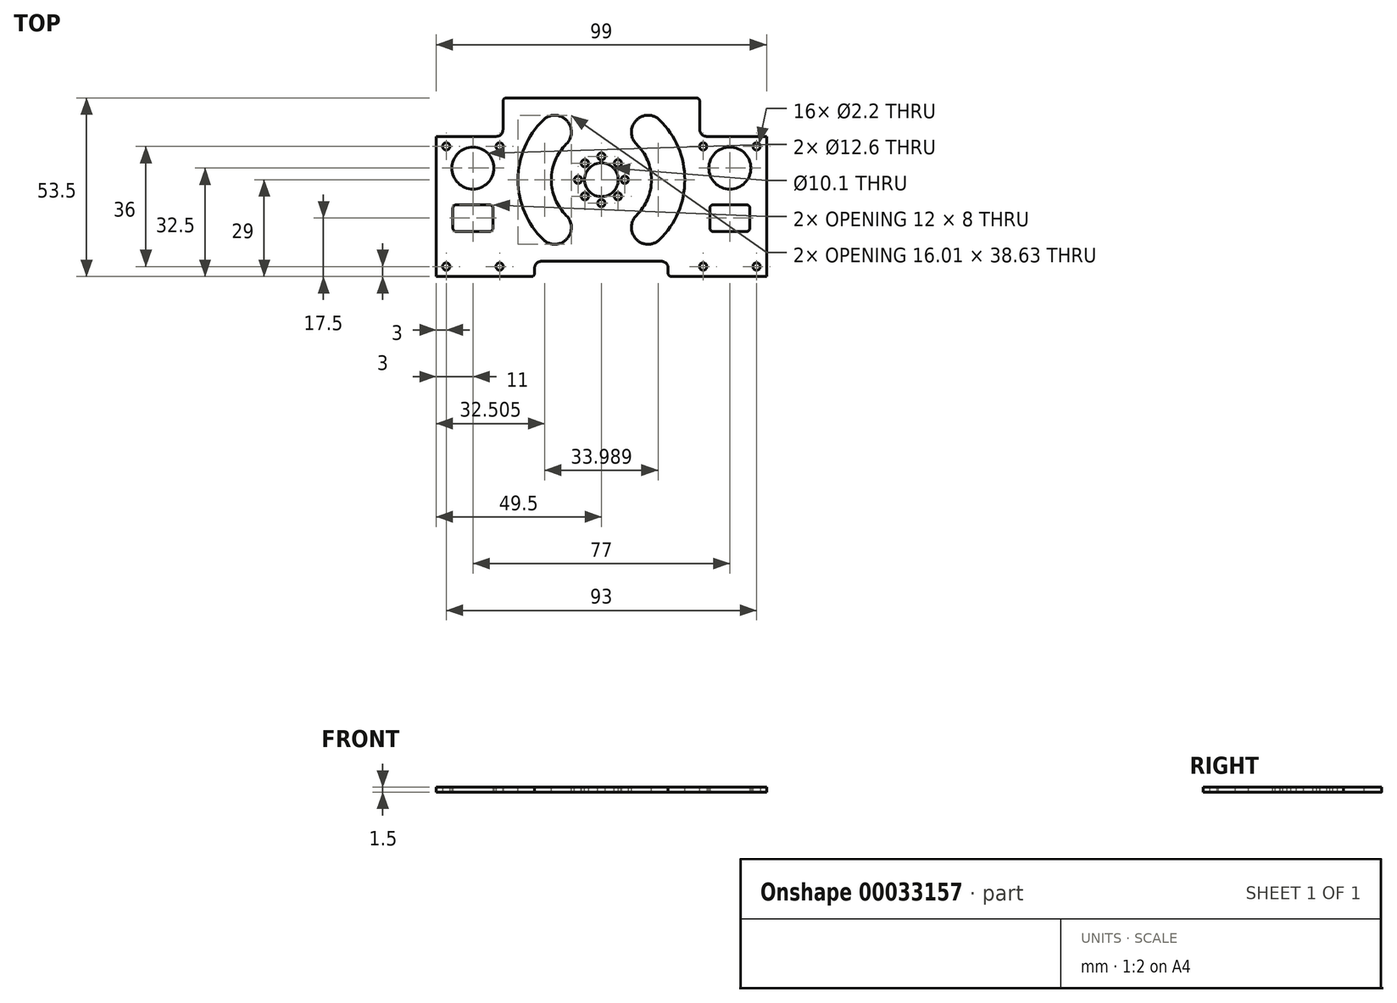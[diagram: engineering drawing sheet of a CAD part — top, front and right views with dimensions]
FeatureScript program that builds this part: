
annotation { "Feature Type Name" : "Feature", "Feature Type Description" : "" }
export const myFeature = defineFeature(function(context is Context, id is Id, definition is map)
    precondition{}
    {
        {
            var Q0;
            Q0=qCreatedBy(makeId("Top.planeOp"),FACE);
            var sketch = newSketch(context, id + "F0", { "sketchPlane" : qUnion([Q0])});
            skLineSegment(sketch, "E0.bottom", {"start": v(-49.5, 35) * mm, "end": v(49.5, 35) * mm});
            skLineSegment(sketch, "E0.top", {"start": v(-49.5, -35) * mm, "end": v(49.5, -35) * mm});
            skLineSegment(sketch, "E0.left", {"start": v(-49.5, 35) * mm, "end": v(-49.5, -35) * mm});
            skLineSegment(sketch, "E0.right", {"start": v(49.5, 35) * mm, "end": v(49.5, -35) * mm});
            skPoint(sketch, "E0.middle", {"position": v(0, 0) * mm});
            skLineSegment(sketch, "E1", {"start": v(-38.5, 35) * mm, "end": v(-38.5, -35) * mm, "construction": true});
            skCircle(sketch, "E2", {"center": v(-46.5, 10) * mm, "radius": 1.1 * mm});
            skCircle(sketch, "E3", {"center": v(-46.5, -26) * mm, "radius": 1.1 * mm});
            skCircle(sketch, "E4.MirrorC", {"center": v(-30.5, 10) * mm, "radius": 1.1 * mm});
            skCircle(sketch, "E5.MirrorC", {"center": v(-30.5, -26) * mm, "radius": 1.1 * mm});
            skCircle(sketch, "E6", {"center": v(-38.5, 3.5) * mm, "radius": 6.3 * mm});
            skCircle(sketch, "E7.MirrorC", {"center": v(30.5, -26) * mm, "radius": 1.1 * mm});
            skCircle(sketch, "E8.MirrorC", {"center": v(38.5, 3.5) * mm, "radius": 6.3 * mm});
            skCircle(sketch, "E9.MirrorC", {"center": v(30.5, 10) * mm, "radius": 1.1 * mm});
            skCircle(sketch, "E10.MirrorC", {"center": v(46.5, 10) * mm, "radius": 1.1 * mm});
            skCircle(sketch, "E11.MirrorC", {"center": v(46.5, -26) * mm, "radius": 1.1 * mm});
            skLineSegment(sketch, "E12.bottom", {"start": v(-33.5, -15.5) * mm, "end": v(-43.5, -15.5) * mm});
            skLineSegment(sketch, "E12.top", {"start": v(-33.5, -7.5) * mm, "end": v(-43.5, -7.5) * mm});
            skLineSegment(sketch, "E12.left", {"start": v(-32.5, -14.5) * mm, "end": v(-32.5, -8.5) * mm});
            skLineSegment(sketch, "E12.right", {"start": v(-44.5, -14.5) * mm, "end": v(-44.5, -8.5) * mm});
            skPoint(sketch, "E12.middle", {"position": v(-38.5, -11.5) * mm});
            skPoint(sketch, "E13.visualSharp", {"position": v(-44.5, -7.5) * mm});
            skArc(sketch, "E13.filletArc", {"start": v(-43.5, -7.5) * mm, "mid": v(-44.2, -7.8) * mm, "end": v(-44.5, -8.5) * mm});
            skPoint(sketch, "E14.visualSharp", {"position": v(-44.5, -15.5) * mm});
            skArc(sketch, "E14.filletArc", {"start": v(-44.5, -14.5) * mm, "mid": v(-44.2, -15.2) * mm, "end": v(-43.5, -15.5) * mm});
            skPoint(sketch, "E15.visualSharp", {"position": v(-32.5, -15.5) * mm});
            skArc(sketch, "E15.filletArc", {"start": v(-33.5, -15.5) * mm, "mid": v(-32.8, -15.2) * mm, "end": v(-32.5, -14.5) * mm});
            skPoint(sketch, "E16.visualSharp", {"position": v(-32.5, -7.5) * mm});
            skArc(sketch, "E16.filletArc", {"start": v(-32.5, -8.5) * mm, "mid": v(-32.8, -7.8) * mm, "end": v(-33.5, -7.5) * mm});
            skArc(sketch, "E17.MirrorCS", {"start": v(43.5, -7.5) * mm, "mid": v(44.2, -7.8) * mm, "end": v(44.5, -8.5) * mm});
            skArc(sketch, "E18.MirrorCS", {"start": v(33.5, -15.5) * mm, "mid": v(32.8, -15.2) * mm, "end": v(32.5, -14.5) * mm});
            skArc(sketch, "E19.MirrorCS", {"start": v(32.5, -8.5) * mm, "mid": v(32.8, -7.8) * mm, "end": v(33.5, -7.5) * mm});
            skArc(sketch, "E20.MirrorCS", {"start": v(44.5, -14.5) * mm, "mid": v(44.2, -15.2) * mm, "end": v(43.5, -15.5) * mm});
            skLineSegment(sketch, "E21.MirrorCS", {"start": v(44.5, -14.5) * mm, "end": v(44.5, -8.5) * mm});
            skLineSegment(sketch, "E22.MirrorCS", {"start": v(33.5, -15.5) * mm, "end": v(43.5, -15.5) * mm});
            skPoint(sketch, "E23.MirrorP", {"position": v(32.5, -15.5) * mm});
            skPoint(sketch, "E24.MirrorP", {"position": v(44.5, -15.5) * mm});
            skPoint(sketch, "E25.MirrorP", {"position": v(44.5, -7.5) * mm});
            skPoint(sketch, "E26.MirrorP", {"position": v(38.5, -11.5) * mm});
            skLineSegment(sketch, "E27.MirrorCS", {"start": v(33.5, -7.5) * mm, "end": v(43.5, -7.5) * mm});
            skLineSegment(sketch, "E28.MirrorCS", {"start": v(32.5, -14.5) * mm, "end": v(32.5, -8.5) * mm});
            skPoint(sketch, "E29.MirrorP", {"position": v(32.5, -7.5) * mm});
            skLineSegment(sketch, "E30", {"start": v(-27.5, 35) * mm, "end": v(-27.5, -35) * mm, "construction": true});
            skArc(sketch, "E31.MirrorCS", {"start": v(-22.5, -8.5) * mm, "mid": v(-22.2, -7.8) * mm, "end": v(-21.5, -7.5) * mm, "construction": true});
            skArc(sketch, "E32.MirrorCS", {"start": v(-10.5, -14.5) * mm, "mid": v(-10.8, -15.2) * mm, "end": v(-11.5, -15.5) * mm, "construction": true});
            skArc(sketch, "E33.MirrorCS", {"start": v(-21.5, -15.5) * mm, "mid": v(-22.2, -15.2) * mm, "end": v(-22.5, -14.5) * mm, "construction": true});
            skArc(sketch, "E34.MirrorCS", {"start": v(-11.5, -7.5) * mm, "mid": v(-10.8, -7.8) * mm, "end": v(-10.5, -8.5) * mm, "construction": true});
            skCircle(sketch, "E35.MirrorC", {"center": v(-8.5, -26) * mm, "radius": 1.1 * mm, "construction": true});
            skCircle(sketch, "E36.MirrorC", {"center": v(-24.5, 10) * mm, "radius": 1.1 * mm, "construction": true});
            skCircle(sketch, "E37.MirrorC", {"center": v(-24.5, -26) * mm, "radius": 1.1 * mm, "construction": true});
            skLineSegment(sketch, "E38.MirrorCS", {"start": v(-10.5, -14.5) * mm, "end": v(-10.5, -8.5) * mm, "construction": true});
            skCircle(sketch, "E39.MirrorC", {"center": v(-16.5, 3.5) * mm, "radius": 6.3 * mm, "construction": true});
            skLineSegment(sketch, "E40.MirrorCS", {"start": v(-21.5, -7.5) * mm, "end": v(-11.5, -7.5) * mm, "construction": true});
            skPoint(sketch, "E41.MirrorP", {"position": v(-16.5, -11.5) * mm});
            skLineSegment(sketch, "E42.MirrorCS", {"start": v(-22.5, -14.5) * mm, "end": v(-22.5, -8.5) * mm, "construction": true});
            skPoint(sketch, "E43.MirrorP", {"position": v(-10.5, -15.5) * mm});
            skPoint(sketch, "E44.MirrorP", {"position": v(-10.5, -7.5) * mm});
            skLineSegment(sketch, "E45.MirrorCS", {"start": v(-21.5, -15.5) * mm, "end": v(-11.5, -15.5) * mm, "construction": true});
            skPoint(sketch, "E46.MirrorP", {"position": v(-22.5, -15.5) * mm});
            skPoint(sketch, "E47.MirrorP", {"position": v(-22.5, -7.5) * mm});
            skCircle(sketch, "E48.MirrorC", {"center": v(-8.5, 10) * mm, "radius": 1.1 * mm, "construction": true});
            skArc(sketch, "E49.MirrorCS", {"start": v(10.5, -14.5) * mm, "mid": v(10.8, -15.2) * mm, "end": v(11.5, -15.5) * mm, "construction": true});
            skArc(sketch, "E50.MirrorCS", {"start": v(21.5, -15.5) * mm, "mid": v(22.2, -15.2) * mm, "end": v(22.5, -14.5) * mm, "construction": true});
            skArc(sketch, "E51.MirrorCS", {"start": v(11.5, -7.5) * mm, "mid": v(10.8, -7.8) * mm, "end": v(10.5, -8.5) * mm, "construction": true});
            skArc(sketch, "E52.MirrorCS", {"start": v(22.5, -8.5) * mm, "mid": v(22.2, -7.8) * mm, "end": v(21.5, -7.5) * mm, "construction": true});
            skLineSegment(sketch, "E53.MirrorCS", {"start": v(10.5, -14.5) * mm, "end": v(10.5, -8.5) * mm, "construction": true});
            skLineSegment(sketch, "E54.MirrorCS", {"start": v(21.5, -15.5) * mm, "end": v(11.5, -15.5) * mm, "construction": true});
            skLineSegment(sketch, "E55.MirrorCS", {"start": v(22.5, -14.5) * mm, "end": v(22.5, -8.5) * mm, "construction": true});
            skPoint(sketch, "E56.MirrorP", {"position": v(10.5, -15.5) * mm});
            skPoint(sketch, "E57.MirrorP", {"position": v(10.5, -7.5) * mm});
            skCircle(sketch, "E58.MirrorC", {"center": v(8.5, -26) * mm, "radius": 1.1 * mm, "construction": true});
            skPoint(sketch, "E59.MirrorP", {"position": v(22.5, -7.5) * mm});
            skCircle(sketch, "E60.MirrorC", {"center": v(8.5, 10) * mm, "radius": 1.1 * mm, "construction": true});
            skLineSegment(sketch, "E61.MirrorCS", {"start": v(21.5, -7.5) * mm, "end": v(11.5, -7.5) * mm, "construction": true});
            skPoint(sketch, "E62.MirrorP", {"position": v(22.5, -15.5) * mm});
            skPoint(sketch, "E63.MirrorP", {"position": v(16.5, -11.5) * mm});
            skCircle(sketch, "E64.MirrorC", {"center": v(16.5, 3.5) * mm, "radius": 6.3 * mm, "construction": true});
            skCircle(sketch, "E65.MirrorC", {"center": v(24.5, 10) * mm, "radius": 1.1 * mm, "construction": true});
            skSolve(sketch);
        }
        {
            var Q0;
            Q0=qSketchRegion(id+"F0",true);
            extrude(context, id + "F1", {"entities" : qUnion([Q0]), "depth" : 1.5 * mm});
        }
        {
            var Q0;
            Q0=makeQuery(id+"F1.opExtrude","CAP_FACE",FACE,{"disambiguationData":[OSD([sQuery(id+"F0.wireOp",EDGE,"E0.bottom"),sQuery(id+"F0.wireOp",EDGE,"E0.top"),sQuery(id+"F0.wireOp",EDGE,"E0.left"),sQuery(id+"F0.wireOp",EDGE,"E0.right"),sQuery(id+"F0.wireOp",EDGE,"E2"),sQuery(id+"F0.wireOp",EDGE,"E3"),sQuery(id+"F0.wireOp",EDGE,"E4.MirrorC"),sQuery(id+"F0.wireOp",EDGE,"E5.MirrorC"),sQuery(id+"F0.wireOp",EDGE,"E6"),sQuery(id+"F0.wireOp",EDGE,"E7.MirrorC"),sQuery(id+"F0.wireOp",EDGE,"E8.MirrorC"),sQuery(id+"F0.wireOp",EDGE,"E9.MirrorC"),sQuery(id+"F0.wireOp",EDGE,"E10.MirrorC"),sQuery(id+"F0.wireOp",EDGE,"E11.MirrorC"),sQuery(id+"F0.wireOp",EDGE,"E12.bottom"),sQuery(id+"F0.wireOp",EDGE,"E12.top"),sQuery(id+"F0.wireOp",EDGE,"E12.left"),sQuery(id+"F0.wireOp",EDGE,"E12.right"),sQuery(id+"F0.wireOp",EDGE,"E13.filletArc"),sQuery(id+"F0.wireOp",EDGE,"E14.filletArc"),sQuery(id+"F0.wireOp",EDGE,"E15.filletArc"),sQuery(id+"F0.wireOp",EDGE,"E16.filletArc"),sQuery(id+"F0.wireOp",EDGE,"E17.MirrorCS"),sQuery(id+"F0.wireOp",EDGE,"E18.MirrorCS"),sQuery(id+"F0.wireOp",EDGE,"E19.MirrorCS"),sQuery(id+"F0.wireOp",EDGE,"E20.MirrorCS"),sQuery(id+"F0.wireOp",EDGE,"E21.MirrorCS"),sQuery(id+"F0.wireOp",EDGE,"E22.MirrorCS"),sQuery(id+"F0.wireOp",EDGE,"E27.MirrorCS"),sQuery(id+"F0.wireOp",EDGE,"E28.MirrorCS"),sQuery(id+"F0.wireOp",EDGE,"zmoQ4JmG-B1Fh-ple2-wA15-Lbddf262ybKt"),sQuery(id+"F0.wireOp",EDGE,"2d430b7b-3c80-43ed-9bf5-037792e47e610.MirrorC"),sQuery(id+"F0.wireOp",EDGE,"38cede9b-45dc-4b58-b28a-d8ac8e4754d90.MirrorC"),sQuery(id+"F0.wireOp",EDGE,"c577f0fc-5771-4c20-9ec0-d27963db61750.MirrorC")])],"isStart":false});
            var sketch = newSketch(context, id + "F2", { "sketchPlane" : qUnion([Q0])});
            skCircle(sketch, "E66", {"center": v(0, 0) * mm, "radius": 5.05 * mm});
            skCircle(sketch, "E67", {"center": v(0, 7) * mm, "radius": 1.1 * mm});
            skCircle(sketch, "E68.1.0", {"center": v(-4.95, 4.95) * mm, "radius": 1.1 * mm});
            skCircle(sketch, "E68.2.0", {"center": v(-7, 0) * mm, "radius": 1.1 * mm});
            skCircle(sketch, "E68.3.0", {"center": v(-4.95, -4.95) * mm, "radius": 1.1 * mm});
            skCircle(sketch, "E68.4.0", {"center": v(0, -7) * mm, "radius": 1.1 * mm});
            skCircle(sketch, "E68.5.0", {"center": v(4.95, -4.95) * mm, "radius": 1.1 * mm});
            skCircle(sketch, "E68.6.0", {"center": v(7, 0) * mm, "radius": 1.1 * mm});
            skCircle(sketch, "E68.7.0", {"center": v(4.95, 4.95) * mm, "radius": 1.1 * mm});
            skArc(sketch, "E69", {"start": v(-17.4, 17.95) * mm, "mid": v(-25, 0) * mm, "end": v(-17.4, -17.95) * mm});
            skArc(sketch, "E70", {"start": v(-10.47, 10.74) * mm, "mid": v(-15, 0) * mm, "end": v(-10.47, -10.74) * mm});
            skLineSegment(sketch, "E71", {"start": v(-9.75, 16.88) * mm, "end": v(-9.64, 16.7) * mm});
            skLineSegment(sketch, "E72.MirrorCS", {"start": v(-9.75, -16.88) * mm, "end": v(-9.64, -16.7) * mm});
            skLineSegment(sketch, "E73.MirrorCS", {"start": v(9.75, 16.88) * mm, "end": v(9.64, 16.7) * mm});
            skLineSegment(sketch, "E74.MirrorCS", {"start": v(9.75, -16.88) * mm, "end": v(9.64, -16.7) * mm});
            skArc(sketch, "E75.trimOffspring", {"start": v(10.47, -10.74) * mm, "mid": v(15, 0) * mm, "end": v(10.47, 10.74) * mm});
            skArc(sketch, "E76.trimOffspring", {"start": v(17.4, -17.95) * mm, "mid": v(25, 0) * mm, "end": v(17.4, 17.95) * mm});
            skPoint(sketch, "E77.visualSharp", {"position": v(-12.5, 21.65) * mm});
            skArc(sketch, "E77.filletArc", {"start": v(-9.75, 16.88) * mm, "mid": v(-13.31, 19.28) * mm, "end": v(-17.4, 17.95) * mm});
            skPoint(sketch, "E78.visualSharp", {"position": v(-7.5, 13) * mm});
            skArc(sketch, "E78.filletArc", {"start": v(-10.47, 10.74) * mm, "mid": v(-9.03, 13.58) * mm, "end": v(-9.64, 16.7) * mm});
            skPoint(sketch, "E79.visualSharp", {"position": v(-7.5, -13) * mm});
            skArc(sketch, "E79.filletArc", {"start": v(-9.64, -16.7) * mm, "mid": v(-9.03, -13.58) * mm, "end": v(-10.47, -10.74) * mm});
            skPoint(sketch, "E80.visualSharp", {"position": v(-12.5, -21.65) * mm});
            skArc(sketch, "E80.filletArc", {"start": v(-17.4, -17.95) * mm, "mid": v(-13.31, -19.28) * mm, "end": v(-9.75, -16.88) * mm});
            skPoint(sketch, "E81.visualSharp", {"position": v(7.5, -13) * mm});
            skArc(sketch, "E81.filletArc", {"start": v(10.47, -10.74) * mm, "mid": v(9.03, -13.58) * mm, "end": v(9.64, -16.7) * mm});
            skPoint(sketch, "E82.visualSharp", {"position": v(12.5, -21.65) * mm});
            skArc(sketch, "E82.filletArc", {"start": v(9.75, -16.88) * mm, "mid": v(13.31, -19.28) * mm, "end": v(17.4, -17.95) * mm});
            skPoint(sketch, "E83.visualSharp", {"position": v(7.5, 13) * mm});
            skArc(sketch, "E83.filletArc", {"start": v(9.64, 16.7) * mm, "mid": v(9.03, 13.58) * mm, "end": v(10.47, 10.74) * mm});
            skPoint(sketch, "E84.visualSharp", {"position": v(12.5, 21.65) * mm});
            skArc(sketch, "E84.filletArc", {"start": v(17.4, 17.95) * mm, "mid": v(13.31, 19.28) * mm, "end": v(9.75, 16.88) * mm});
            skLineSegment(sketch, "E85.bottom", {"start": v(-49.5, 35) * mm, "end": v(-29.5, 35) * mm});
            skLineSegment(sketch, "E85.top", {"start": v(-49.5, 13) * mm, "end": v(-31.5, 13) * mm});
            skLineSegment(sketch, "E85.left", {"start": v(-49.5, 35) * mm, "end": v(-49.5, 13) * mm});
            skLineSegment(sketch, "E85.right", {"start": v(-29.5, 35) * mm, "end": v(-29.5, 15) * mm});
            skPoint(sketch, "E86", {"position": v(-26.5, 21.5) * mm});
            skPoint(sketch, "E87", {"position": v(-30.5, 10) * mm});
            skLineSegment(sketch, "E88.MirrorCS", {"start": v(49.5, 13) * mm, "end": v(31.5, 13) * mm});
            skLineSegment(sketch, "E89.MirrorCS", {"start": v(49.5, 35) * mm, "end": v(29.5, 35) * mm});
            skPoint(sketch, "E90.MirrorP", {"position": v(26.5, 21.5) * mm});
            skLineSegment(sketch, "E91.MirrorCS", {"start": v(29.5, 35) * mm, "end": v(29.5, 15) * mm});
            skLineSegment(sketch, "E92.MirrorCS", {"start": v(49.5, 35) * mm, "end": v(49.5, 13) * mm});
            skPoint(sketch, "E93.MirrorP", {"position": v(30.5, 10) * mm});
            skPoint(sketch, "E94.visualSharp", {"position": v(-29.5, 13) * mm});
            skArc(sketch, "E94.filletArc", {"start": v(-31.5, 13) * mm, "mid": v(-30.09, 13.59) * mm, "end": v(-29.5, 15) * mm});
            skPoint(sketch, "E95.visualSharp", {"position": v(29.5, 13) * mm});
            skArc(sketch, "E95.filletArc", {"start": v(29.5, 15) * mm, "mid": v(30.09, 13.59) * mm, "end": v(31.5, 13) * mm});
            skLineSegment(sketch, "E96.bottom", {"start": v(-29.5, 35) * mm, "end": v(29.5, 35) * mm});
            skLineSegment(sketch, "E96.top", {"start": v(-29.5, 24.5) * mm, "end": v(29.5, 24.5) * mm});
            skLineSegment(sketch, "E96.left", {"start": v(-29.5, 35) * mm, "end": v(-29.5, 24.5) * mm});
            skLineSegment(sketch, "E96.right", {"start": v(29.5, 35) * mm, "end": v(29.5, 24.5) * mm});
            skLineSegment(sketch, "E97.bottom", {"start": v(20, -35) * mm, "end": v(-20, -35) * mm});
            skLineSegment(sketch, "E97.top", {"start": v(20, -24.43) * mm, "end": v(-20, -24.43) * mm});
            skLineSegment(sketch, "E97.left", {"start": v(20, -35) * mm, "end": v(20, -24.43) * mm});
            skLineSegment(sketch, "E97.right", {"start": v(-20, -35) * mm, "end": v(-20, -24.43) * mm});
            skPoint(sketch, "E97.middle", {"position": v(0, -29.72) * mm});
            skLineSegment(sketch, "E98.bottom", {"start": v(-49.5, -35) * mm, "end": v(-20, -35) * mm});
            skLineSegment(sketch, "E98.top", {"start": v(-49.5, -29) * mm, "end": v(-20, -29) * mm});
            skLineSegment(sketch, "E98.left", {"start": v(-49.5, -35) * mm, "end": v(-49.5, -29) * mm});
            skLineSegment(sketch, "E98.right", {"start": v(-20, -35) * mm, "end": v(-20, -29) * mm});
            skPoint(sketch, "E99", {"position": v(-30.5, -26) * mm});
            skLineSegment(sketch, "E100.MirrorCS", {"start": v(49.5, -29) * mm, "end": v(20, -29) * mm});
            skLineSegment(sketch, "E101.MirrorCS", {"start": v(49.5, -35) * mm, "end": v(49.5, -29) * mm});
            skLineSegment(sketch, "E102.MirrorCS", {"start": v(49.5, -35) * mm, "end": v(20, -35) * mm});
            skSolve(sketch);
        }
        {
            var Q0;
            Q0 = qSketchRegion(id + "F2", true);
            extrude(context, id + "F3", {"entities" : qUnion([Q0]), "operationType" : NewBodyOperationType.REMOVE, "endBound" : BoundingType.UP_TO_NEXT, "oppositeDirection" : true, "depth" : 25 * mm});
        }
        {
            var Q0;
            Q0=makeQuery(id+"F3.boolean.opBoolean","COPY",EDGE,{"derivedFrom":makeQuery(id+"F3.opExtrude","SWEPT_EDGE",EDGE,{"disambiguationData":[OSD([sQuery(id+"F2.wireOp",EDGE,"E97.top"),sQuery(id+"F2.wireOp",EDGE,"E97.right")])]})});
            var Q1;
            Q1=makeQuery(id+"F3.boolean.opBoolean","COPY",EDGE,{"derivedFrom":makeQuery(id+"F3.opExtrude","SWEPT_EDGE",EDGE,{"disambiguationData":[OSD([sQuery(id+"F2.wireOp",EDGE,"E97.top"),sQuery(id+"F2.wireOp",EDGE,"E97.left")])]})});
            fillet(context, id + "F4", {"entities" : qUnion([Q0, Q1]), "radius" : 2 * mm, "tangentPropagation" : true, "allowEdgeOverflow" : false});
        }
        {
            var Q0;
            Q0=makeQuery(id+"F3.boolean.opBoolean","COPY",EDGE,{"derivedFrom":makeQuery(id+"F3.opExtrude","SWEPT_EDGE",EDGE,{"disambiguationData":[OSD([sQuery(id+"F0.wireOp",EDGE,"E0.left"),sQuery(id+"F2.wireOp",EDGE,"E98.top"),sQuery(id+"F2.wireOp",EDGE,"E98.left")])]})});
            var Q1;
            Q1=makeQuery(id+"F3.boolean.opBoolean","COPY",EDGE,{"derivedFrom":makeQuery(id+"F3.opExtrude","SWEPT_EDGE",EDGE,{"disambiguationData":[OSD([sQuery(id+"F2.wireOp",EDGE,"E97.left"),sQuery(id+"F2.wireOp",EDGE,"E100.MirrorCS")])]})});
            var Q2;
            Q2=makeQuery(id+"F3.boolean.opBoolean","COPY",EDGE,{"derivedFrom":makeQuery(id+"F3.opExtrude","SWEPT_EDGE",EDGE,{"disambiguationData":[OSD([sQuery(id+"F2.wireOp",EDGE,"E97.right"),sQuery(id+"F2.wireOp",EDGE,"E98.top"),sQuery(id+"F2.wireOp",EDGE,"E98.right")])]})});
            var Q3;
            Q3=makeQuery(id+"F3.boolean.opBoolean","COPY",EDGE,{"derivedFrom":makeQuery(id+"F3.opExtrude","SWEPT_EDGE",EDGE,{"disambiguationData":[OSD([sQuery(id+"F0.wireOp",EDGE,"E0.right"),sQuery(id+"F2.wireOp",EDGE,"E100.MirrorCS"),sQuery(id+"F2.wireOp",EDGE,"E101.MirrorCS")])]})});
            var Q4;
            Q4=makeQuery(id+"F3.boolean.opBoolean","COPY",EDGE,{"derivedFrom":makeQuery(id+"F3.opExtrude","SWEPT_EDGE",EDGE,{"disambiguationData":[OSD([sQuery(id+"F0.wireOp",EDGE,"E0.right"),sQuery(id+"F2.wireOp",EDGE,"E88.MirrorCS"),sQuery(id+"F2.wireOp",EDGE,"E92.MirrorCS")])]})});
            var Q5;
            Q5=makeQuery(id+"F3.boolean.opBoolean","COPY",EDGE,{"derivedFrom":makeQuery(id+"F3.opExtrude","SWEPT_EDGE",EDGE,{"disambiguationData":[OSD([sQuery(id+"F2.wireOp",EDGE,"E91.MirrorCS"),sQuery(id+"F2.wireOp",EDGE,"E96.top"),sQuery(id+"F2.wireOp",EDGE,"E96.right")])]})});
            var Q6;
            Q6=makeQuery(id+"F3.boolean.opBoolean","COPY",EDGE,{"derivedFrom":makeQuery(id+"F3.opExtrude","SWEPT_EDGE",EDGE,{"disambiguationData":[OSD([sQuery(id+"F0.wireOp",EDGE,"E0.left"),sQuery(id+"F2.wireOp",EDGE,"E85.top"),sQuery(id+"F2.wireOp",EDGE,"E85.left")])]})});
            var Q7;
            Q7=makeQuery(id+"F3.boolean.opBoolean","COPY",EDGE,{"derivedFrom":makeQuery(id+"F3.opExtrude","SWEPT_EDGE",EDGE,{"disambiguationData":[OSD([sQuery(id+"F2.wireOp",EDGE,"E85.right"),sQuery(id+"F2.wireOp",EDGE,"E96.top"),sQuery(id+"F2.wireOp",EDGE,"E96.left")])]})});
            fillet(context, id + "F5", {"entities" : qUnion([Q0, Q1, Q2, Q3, Q4, Q5, Q6, Q7]), "radius" : 1 * mm, "tangentPropagation" : true, "allowEdgeOverflow" : false});
        }
    });
